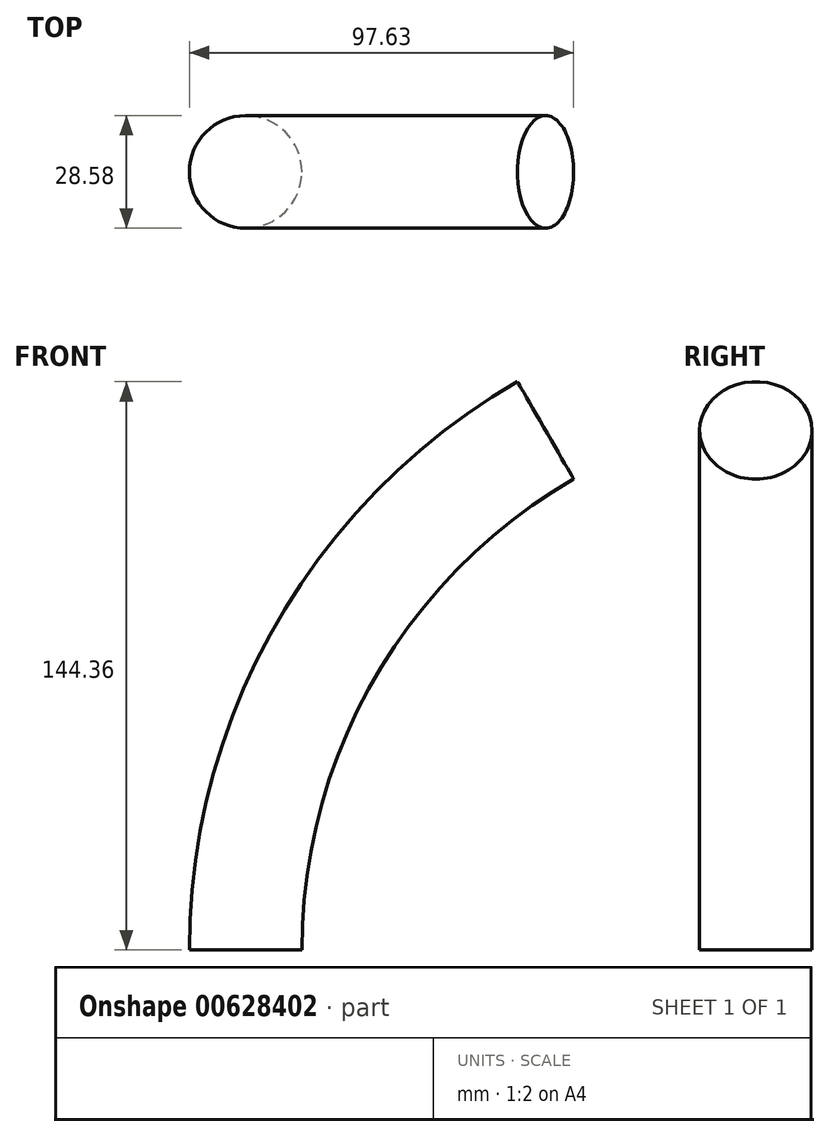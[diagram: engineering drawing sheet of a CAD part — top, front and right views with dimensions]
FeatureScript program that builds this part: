
annotation { "Feature Type Name" : "Feature", "Feature Type Description" : "" }
export const myFeature = defineFeature(function(context is Context, id is Id, definition is map)
    precondition{}
    {
        {
            var Q0;
            Q0=qCreatedBy(makeId("Top.planeOp"),FACE);
            var sketch = newSketch(context, id + "F0", { "sketchPlane" : qUnion([Q0])});
            skLineSegment(sketch, "E0", {"start": v(0, 156.97) * mm, "end": v(0, 0) * mm});
            skLineSegment(sketch, "E1", {"start": v(0, 0) * mm, "end": v(0, -158.22) * mm});
            skLineSegment(sketch, "E2", {"start": v(0, 0) * mm, "end": v(-152.4, 0) * mm});
            skCircle(sketch, "E3", {"center": v(-152.4, 0) * mm, "radius": 14.29 * mm});
            skSolve(sketch);
        }
        {
            var Q0;
            Q0=makeQuery(id+"F0.imprint","IMPRINT",FACE,{"disambiguationData":[TD([[makeQuery(id+"F0.imprint","IMPRINT",EDGE,{"derivedFrom":sQuery(id+"F0.wireOp",EDGE,"E3")}),1.0]])]});
            var Q1;
            Q1=sQuery(id+"F0.wireOp",EDGE,"E1");
            revolve(context, id + "F1", {"entities" : qUnion([Q0]), "axis" : qUnion([Q1]), "revolveType" : RevolveType.ONE_DIRECTION, "oppositeDirection" : true, "angle" : 60 * degree});
        }
    });
